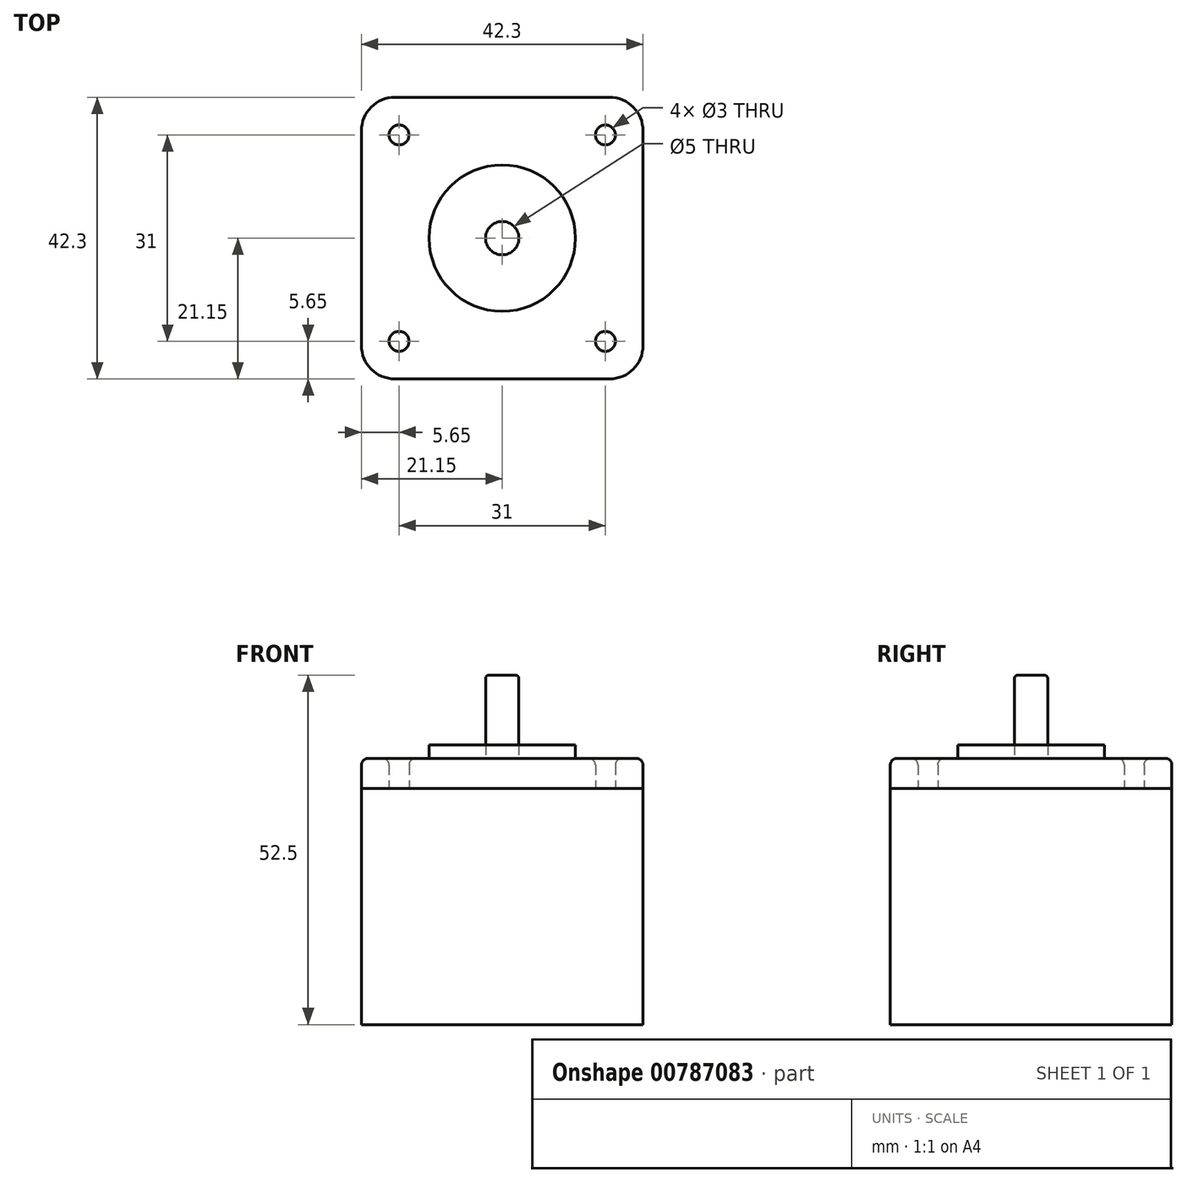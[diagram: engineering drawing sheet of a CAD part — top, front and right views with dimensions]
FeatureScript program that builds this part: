
annotation { "Feature Type Name" : "Feature", "Feature Type Description" : "" }
export const myFeature = defineFeature(function(context is Context, id is Id, definition is map)
    precondition{}
    {
        {
            var Q0;
            Q0=qCreatedBy(makeId("Top.planeOp"),FACE);
            var sketch = newSketch(context, id + "F0", { "sketchPlane" : qUnion([Q0])});
            skLineSegment(sketch, "E0.bottom", {"start": v(-21.15, -21.15) * mm, "end": v(21.15, -21.15) * mm});
            skLineSegment(sketch, "E0.top", {"start": v(-21.15, 21.15) * mm, "end": v(21.15, 21.15) * mm});
            skLineSegment(sketch, "E0.left", {"start": v(-21.15, -21.15) * mm, "end": v(-21.15, 21.15) * mm});
            skLineSegment(sketch, "E0.right", {"start": v(21.15, -21.15) * mm, "end": v(21.15, 21.15) * mm});
            skPoint(sketch, "E0.middle", {"position": v(0, 0) * mm});
            skSolve(sketch);
        }
        {
            var Q0;
            Q0=makeQuery(id+"F0.imprint","IMPRINT",FACE,{"disambiguationData":[TD([[makeQuery(id+"F0.imprint","IMPRINT",EDGE,{"derivedFrom":sQuery(id+"F0.wireOp",EDGE,"E0.bottom")}),1.0]])]});
            extrude(context, id + "F1", {"entities" : qUnion([Q0]), "depth" : 43.5 * mm, "offsetDistance" : 25 * mm});
        }
        {
            var Q0;
            Q0=makeQuery(id+"F0.imprint","IMPRINT",FACE,{"disambiguationData":[TD([[makeQuery(id+"F0.imprint","IMPRINT",EDGE,{"derivedFrom":sQuery(id+"F0.wireOp",EDGE,"E0.bottom")}),1.0]])]});
            var sketch = newSketch(context, id + "F2", { "sketchPlane" : qUnion([Q0])});
            skLineSegment(sketch, "E1.bottom", {"start": v(-15.5, -15.5) * mm, "end": v(15.5, -15.5) * mm, "construction": true});
            skLineSegment(sketch, "E1.top", {"start": v(-15.5, 15.5) * mm, "end": v(15.5, 15.5) * mm, "construction": true});
            skLineSegment(sketch, "E1.left", {"start": v(-15.5, -15.5) * mm, "end": v(-15.5, 15.5) * mm, "construction": true});
            skLineSegment(sketch, "E1.right", {"start": v(15.5, -15.5) * mm, "end": v(15.5, 15.5) * mm, "construction": true});
            skPoint(sketch, "E1.middle", {"position": v(0, 0) * mm});
            skCircle(sketch, "E2", {"center": v(15.5, -15.5) * mm, "radius": 1.5 * mm});
            skCircle(sketch, "E3", {"center": v(-15.5, -15.5) * mm, "radius": 1.5 * mm});
            skCircle(sketch, "E4", {"center": v(-15.5, 15.5) * mm, "radius": 1.5 * mm});
            skCircle(sketch, "E5", {"center": v(15.5, 15.5) * mm, "radius": 1.5 * mm});
            skSolve(sketch);
        }
        {
            var Q0;
            {var subQ0=sQuery(id+"F2.wireOp",EDGE,"E1.left");var subQ1=sQuery(id+"F2.wireOp",EDGE,"E1.bottom");var subQ2=makeQuery(id+"F2.imprint","INTERSECT",VERTEX,{"derivedFrom":[subQ1,subQ0]});Q0=makeQuery(id+"F2.imprint","IMPRINT",FACE,{"disambiguationData":[TD([[makeQuery(id+"F2.imprint","IMPRINT",EDGE,{"disambiguationData":[TD([[subQ2,-1.0]])],"derivedFrom":subQ1}),-1.0]])]});}
            var Q1;
            {var subQ0=sQuery(id+"F2.wireOp",EDGE,"E1.right");var subQ1=sQuery(id+"F2.wireOp",EDGE,"E1.bottom");var subQ2=makeQuery(id+"F2.imprint","INTERSECT",VERTEX,{"derivedFrom":[subQ1,subQ0]});Q1=makeQuery(id+"F2.imprint","IMPRINT",FACE,{"disambiguationData":[TD([[makeQuery(id+"F2.imprint","IMPRINT",EDGE,{"disambiguationData":[TD([[subQ2,1.0]])],"derivedFrom":subQ1}),-1.0]])]});}
            var Q2;
            {var subQ0=sQuery(id+"F2.wireOp",EDGE,"E1.right");var subQ1=sQuery(id+"F2.wireOp",EDGE,"E1.top");var subQ2=makeQuery(id+"F2.imprint","INTERSECT",VERTEX,{"derivedFrom":[subQ1,subQ0]});Q2=makeQuery(id+"F2.imprint","IMPRINT",FACE,{"disambiguationData":[TD([[makeQuery(id+"F2.imprint","IMPRINT",EDGE,{"disambiguationData":[TD([[subQ2,1.0]])],"derivedFrom":subQ1}),1.0]])]});}
            var Q3;
            {var subQ0=sQuery(id+"F2.wireOp",EDGE,"E1.left");var subQ1=sQuery(id+"F2.wireOp",EDGE,"E1.top");var subQ2=makeQuery(id+"F2.imprint","INTERSECT",VERTEX,{"derivedFrom":[subQ1,subQ0]});Q3=makeQuery(id+"F2.imprint","IMPRINT",FACE,{"disambiguationData":[TD([[makeQuery(id+"F2.imprint","IMPRINT",EDGE,{"disambiguationData":[TD([[subQ2,-1.0]])],"derivedFrom":subQ1}),1.0]])]});}
            var Q4;
            {var subQ5=sQuery(id+"F2.wireOp",EDGE,"E3");var subQ13=sQuery(id+"F2.wireOp",EDGE,"E1.bottom");var subQ14=makeQuery(id+"F2.imprint","INTERSECT",VERTEX,{"derivedFrom":[subQ13,subQ5]});Q4=makeQuery(id+"F2.imprint","IMPRINT",FACE,{"disambiguationData":[TD([[makeQuery(id+"F2.imprint","IMPRINT",EDGE,{"disambiguationData":[TD([[subQ14,-1.0]])],"derivedFrom":subQ13}),1.0]])]});}
            var Q5;
            Q5=makeQuery(id+"F2.imprint","IMPRINT",FACE,{"disambiguationData":[TD([[makeQuery(id+"F2.imprint","IMPRINT",EDGE,{"derivedFrom":makeQuery(id+"F0.imprint","IMPRINT",EDGE,{"derivedFrom":sQuery(id+"F0.wireOp",EDGE,"E0.bottom")})}),1.0]])]});
            extrude(context, id + "F3", {"entities" : qUnion([Q0, Q1, Q2, Q3, Q4, Q5]), "depth" : 48 * mm, "offsetDistance" : 25 * mm, "hasSecondDirection" : true, "secondDirectionOppositeDirection" : false, "secondDirectionDepth" : 43.5 * mm});
        }
        {
            var Q0;
            Q0=makeQuery(id+"F3.opExtrude","CAP_FACE",FACE,{"disambiguationData":[OSD([sQuery(id+"F0.wireOp",EDGE,"E0.bottom"),sQuery(id+"F0.wireOp",EDGE,"E0.top"),sQuery(id+"F0.wireOp",EDGE,"E0.left"),sQuery(id+"F0.wireOp",EDGE,"E0.right"),sQuery(id+"F2.wireOp",EDGE,"E2"),sQuery(id+"F2.wireOp",EDGE,"E3"),sQuery(id+"F2.wireOp",EDGE,"E4"),sQuery(id+"F2.wireOp",EDGE,"E5")])],"isStart":false});
            var sketch = newSketch(context, id + "F4", { "sketchPlane" : qUnion([Q0])});
            skCircle(sketch, "E6", {"center": v(0, 0) * mm, "radius": 2.5 * mm});
            skCircle(sketch, "E7", {"center": v(0, 0) * mm, "radius": 11 * mm});
            skSolve(sketch);
        }
        {
            var Q0;
            Q0=makeQuery(id+"F4.imprint","IMPRINT",FACE,{"disambiguationData":[TD([[makeQuery(id+"F4.imprint","IMPRINT",EDGE,{"derivedFrom":sQuery(id+"F4.wireOp",EDGE,"E6")}),1.0]])]});
            extrude(context, id + "F5", {"entities" : qUnion([Q0]), "depth" : 12.5 * mm, "offsetDistance" : 25 * mm});
        }
        {
            var Q0;
            Q0=makeQuery(id+"F4.imprint","IMPRINT",FACE,{"disambiguationData":[TD([[makeQuery(id+"F4.imprint","IMPRINT",EDGE,{"derivedFrom":sQuery(id+"F4.wireOp",EDGE,"E6")}),-1.0]])]});
            extrude(context, id + "F6", {"entities" : qUnion([Q0]), "depth" : 2 * mm, "offsetDistance" : 25 * mm});
        }
        {
            var Q0;
            Q0=makeQuery(id+"F5.opExtrude","CAP_EDGE",EDGE,{"disambiguationData":[OSD([sQuery(id+"F4.wireOp",EDGE,"E6")])],"isStart":false});
            fillet(context, id + "F7", {"entities" : qUnion([Q0]), "radius" : 0.5 * mm, "tangentPropagation" : true, "allowEdgeOverflow" : false});
        }
        {
            var Q0;
            Q0=makeQuery(id+"F1.opExtrude","SWEPT_EDGE",EDGE,{"disambiguationData":[OSD([sQuery(id+"F0.wireOp",EDGE,"E0.top"),sQuery(id+"F0.wireOp",EDGE,"E0.left")])]});
            var Q1;
            Q1=makeQuery(id+"F1.opExtrude","SWEPT_EDGE",EDGE,{"disambiguationData":[OSD([sQuery(id+"F0.wireOp",EDGE,"E0.top"),sQuery(id+"F0.wireOp",EDGE,"E0.right")])]});
            var Q2;
            Q2=makeQuery(id+"F3.opExtrude","SWEPT_EDGE",EDGE,{"disambiguationData":[OSD([sQuery(id+"F0.wireOp",EDGE,"E0.top"),sQuery(id+"F0.wireOp",EDGE,"E0.right")])]});
            var Q3;
            Q3=makeQuery(id+"F3.opExtrude","SWEPT_EDGE",EDGE,{"disambiguationData":[OSD([sQuery(id+"F0.wireOp",EDGE,"E0.top"),sQuery(id+"F0.wireOp",EDGE,"E0.left")])]});
            var Q4;
            Q4=makeQuery(id+"F1.opExtrude","SWEPT_EDGE",EDGE,{"disambiguationData":[OSD([sQuery(id+"F0.wireOp",EDGE,"E0.bottom"),sQuery(id+"F0.wireOp",EDGE,"E0.left")])]});
            var Q5;
            Q5=makeQuery(id+"F3.opExtrude","SWEPT_EDGE",EDGE,{"disambiguationData":[OSD([sQuery(id+"F0.wireOp",EDGE,"E0.bottom"),sQuery(id+"F0.wireOp",EDGE,"E0.left")])]});
            var Q6;
            Q6=makeQuery(id+"F3.opExtrude","SWEPT_EDGE",EDGE,{"disambiguationData":[OSD([sQuery(id+"F0.wireOp",EDGE,"E0.bottom"),sQuery(id+"F0.wireOp",EDGE,"E0.right")])]});
            var Q7;
            Q7=makeQuery(id+"F1.opExtrude","SWEPT_EDGE",EDGE,{"disambiguationData":[OSD([sQuery(id+"F0.wireOp",EDGE,"E0.bottom"),sQuery(id+"F0.wireOp",EDGE,"E0.right")])]});
            fillet(context, id + "F8", {"entities" : qUnion([Q0, Q1, Q2, Q3, Q4, Q5, Q6, Q7]), "radius" : 5 * mm, "tangentPropagation" : true, "allowEdgeOverflow" : false});
        }
        {
            var Q0;
            Q0=makeQuery(id+"F1.opExtrude","CAP_FACE",FACE,{"disambiguationData":[OSD([sQuery(id+"F0.wireOp",EDGE,"E0.bottom"),sQuery(id+"F0.wireOp",EDGE,"E0.top"),sQuery(id+"F0.wireOp",EDGE,"E0.left"),sQuery(id+"F0.wireOp",EDGE,"E0.right")])],"isStart":true});
            var Q1;
            Q1=makeQuery(id+"F3.opExtrude","CAP_FACE",FACE,{"disambiguationData":[OSD([sQuery(id+"F0.wireOp",EDGE,"E0.bottom"),sQuery(id+"F0.wireOp",EDGE,"E0.top"),sQuery(id+"F0.wireOp",EDGE,"E0.left"),sQuery(id+"F0.wireOp",EDGE,"E0.right"),sQuery(id+"F2.wireOp",EDGE,"E2"),sQuery(id+"F2.wireOp",EDGE,"E3"),sQuery(id+"F2.wireOp",EDGE,"E4"),sQuery(id+"F2.wireOp",EDGE,"E5")])],"isStart":false});
            fillet(context, id + "F9", {"entities" : qUnion([Q0, Q1]), "radius" : 1 * mm, "tangentPropagation" : true, "allowEdgeOverflow" : false});
        }
        {
            var Q0;
            Q0=makeQuery(id+"F1.opExtrude","CAP_FACE",FACE,{"disambiguationData":[OSD([sQuery(id+"F0.wireOp",EDGE,"E0.bottom"),sQuery(id+"F0.wireOp",EDGE,"E0.top"),sQuery(id+"F0.wireOp",EDGE,"E0.left"),sQuery(id+"F0.wireOp",EDGE,"E0.right")])],"isStart":true});
            var sketch = newSketch(context, id + "F10", { "sketchPlane" : qUnion([Q0])});
            skLineSegment(sketch, "E8.bottom", {"start": v(22.61, 22.68) * mm, "end": v(-22.61, 22.68) * mm});
            skLineSegment(sketch, "E8.top", {"start": v(22.61, -22.68) * mm, "end": v(-22.61, -22.68) * mm});
            skLineSegment(sketch, "E8.left", {"start": v(22.61, 22.68) * mm, "end": v(22.61, -22.68) * mm});
            skLineSegment(sketch, "E8.right", {"start": v(-22.61, 22.68) * mm, "end": v(-22.61, -22.68) * mm});
            skPoint(sketch, "E8.middle", {"position": v(0, 0) * mm});
            skSolve(sketch);
        }
        {
            var Q0;
            Q0 = qSketchRegion(id + "F10", true);
            extrude(context, id + "F11", {"entities" : qUnion([Q0]), "operationType" : NewBodyOperationType.REMOVE, "oppositeDirection" : true, "depth" : 8 * mm, "offsetDistance" : 25 * mm});
        }
    });
